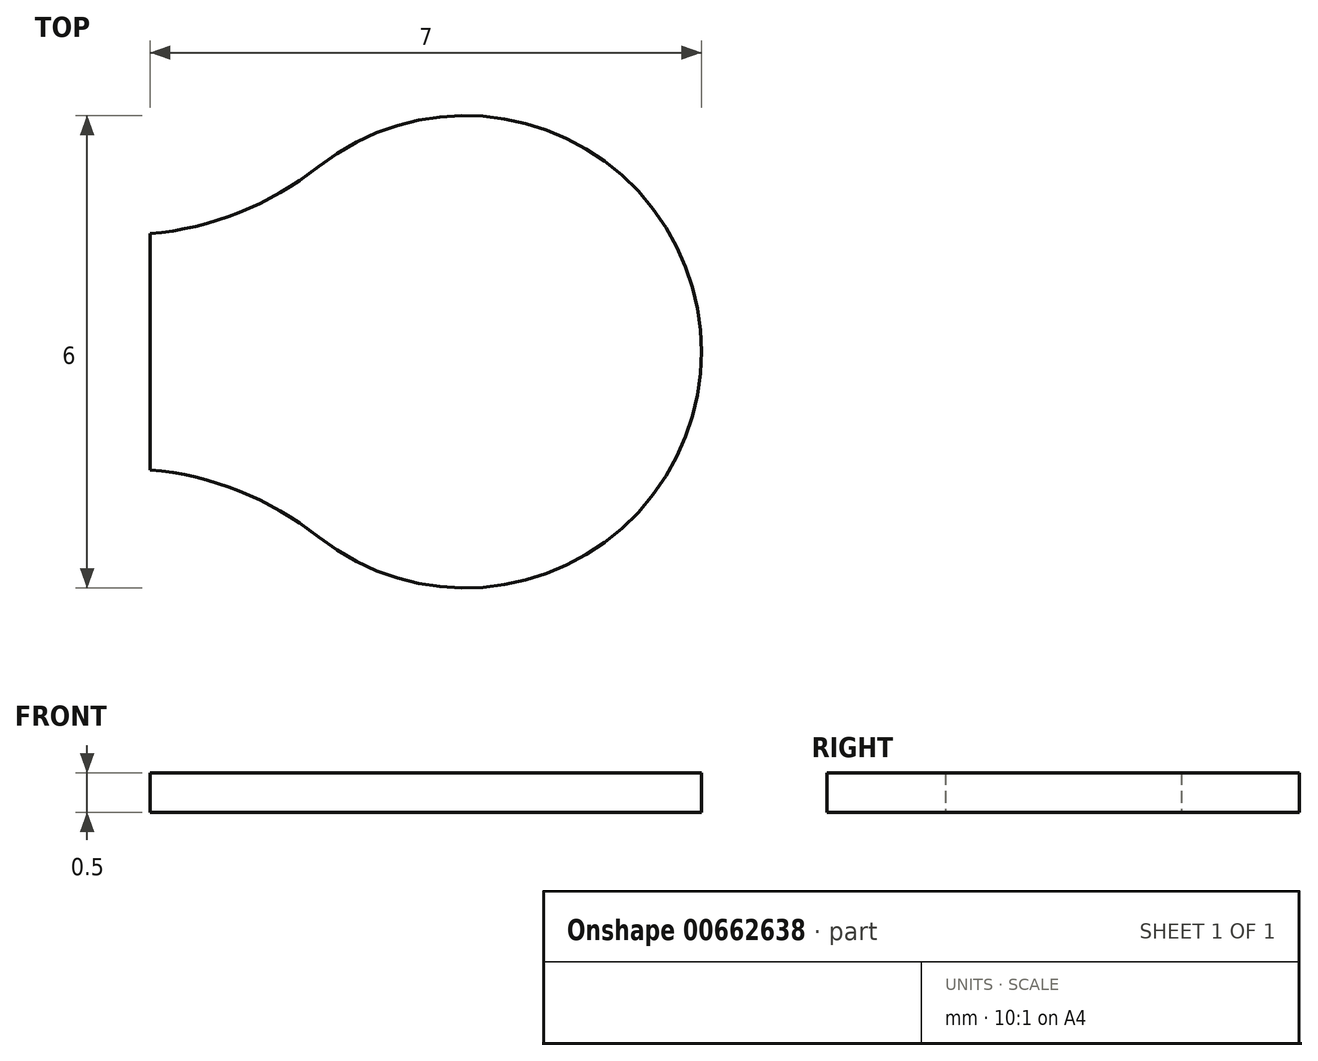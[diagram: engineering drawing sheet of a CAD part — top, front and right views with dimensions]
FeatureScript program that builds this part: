
annotation { "Feature Type Name" : "Feature", "Feature Type Description" : "" }
export const myFeature = defineFeature(function(context is Context, id is Id, definition is map)
    precondition{}
    {
        {
            var Q0;
            Q0=qCreatedBy(makeId("Top.planeOp"),FACE);
            var sketch = newSketch(context, id + "F0", { "sketchPlane" : qUnion([Q0])});
            skArc(sketch, "E0", {"start": v(-1.86, -2.35) * mm, "mid": v(3, 0) * mm, "end": v(-1.86, 2.35) * mm});
            skLineSegment(sketch, "E1", {"start": v(-4, 1.5) * mm, "end": v(-4, -1.5) * mm});
            skPoint(sketch, "E2.third.point", {"position": v(-0.5, 4.36) * mm});
            skArc(sketch, "E3", {"start": v(-1.86, 2.35) * mm, "mid": v(-2.87, 1.77) * mm, "end": v(-4, 1.5) * mm});
            skArc(sketch, "E4.MirrorCS", {"start": v(-1.86, -2.35) * mm, "mid": v(-2.87, -1.77) * mm, "end": v(-4, -1.5) * mm});
            skSolve(sketch);
        }
        {
            var Q0;
            Q0=makeQuery(id+"F0.imprint","IMPRINT",FACE,{"disambiguationData":[TD([[makeQuery(id+"F0.imprint","IMPRINT",EDGE,{"derivedFrom":sQuery(id+"F0.wireOp",EDGE,"E0")}),1.0]])]});
            extrude(context, id + "F1", {"entities" : qUnion([Q0]), "depth" : .5 * mm, "offsetDistance" : 25 * mm});
        }
    });
